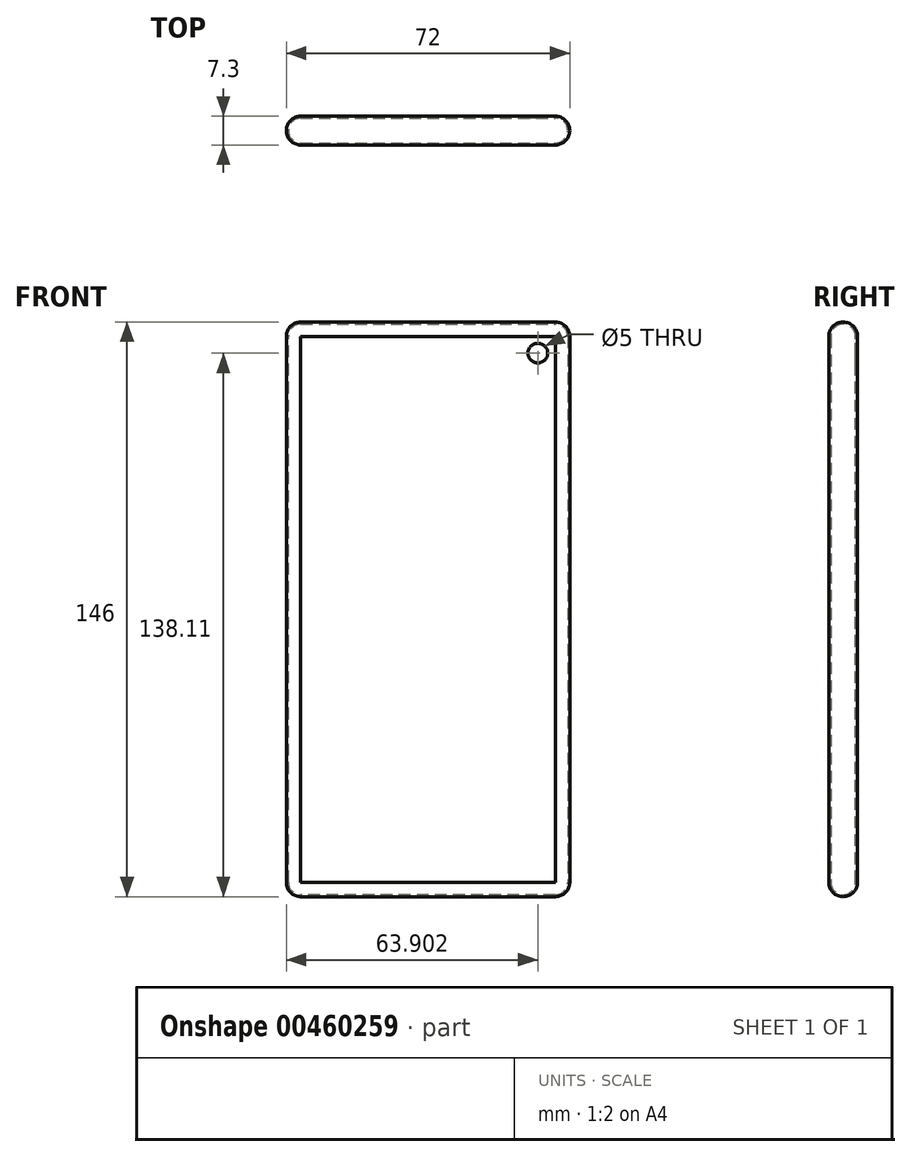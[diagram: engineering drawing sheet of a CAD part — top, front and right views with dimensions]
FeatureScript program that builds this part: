
annotation { "Feature Type Name" : "Feature", "Feature Type Description" : "" }
export const myFeature = defineFeature(function(context is Context, id is Id, definition is map)
    precondition{}
    {
        {
            var Q0;
            Q0=qCreatedBy(makeId("Front.planeOp"),FACE);
            var sketch = newSketch(context, id + "F0", { "sketchPlane" : qUnion([Q0])});
            skLineSegment(sketch, "E0.bottom", {"start": v(36, -73) * mm, "end": v(-36, -73) * mm});
            skLineSegment(sketch, "E0.top", {"start": v(36, 73) * mm, "end": v(-36, 73) * mm});
            skLineSegment(sketch, "E0.left", {"start": v(36, -73) * mm, "end": v(36, 73) * mm});
            skLineSegment(sketch, "E0.right", {"start": v(-36, -73) * mm, "end": v(-36, 73) * mm});
            skPoint(sketch, "E0.middle", {"position": v(0, 0) * mm});
            skSolve(sketch);
        }
        {
            var Q0;
            Q0 = qSketchRegion(id + "F0", true);
            extrude(context, id + "F1", {"entities" : qUnion([Q0]), "depth" : 7.3 * mm, "symmetric" : true});
        }
        {
            var Q0;
            Q0=makeQuery(id+"F1.opExtrude","CAP_EDGE",EDGE,{"disambiguationData":[OSD([sQuery(id+"F0.wireOp",EDGE,"E0.top")])],"isStart":false});
            var Q1;
            Q1=makeQuery(id+"F1.opExtrude","CAP_EDGE",EDGE,{"disambiguationData":[OSD([sQuery(id+"F0.wireOp",EDGE,"E0.top")])],"isStart":true});
            var Q2;
            Q2=makeQuery(id+"F1.opExtrude","CAP_EDGE",EDGE,{"disambiguationData":[OSD([sQuery(id+"F0.wireOp",EDGE,"E0.bottom")])],"isStart":false});
            var Q3;
            Q3=makeQuery(id+"F1.opExtrude","CAP_EDGE",EDGE,{"disambiguationData":[OSD([sQuery(id+"F0.wireOp",EDGE,"E0.bottom")])],"isStart":true});
            var Q4;
            Q4=makeQuery(id+"F1.opExtrude","CAP_EDGE",EDGE,{"disambiguationData":[OSD([sQuery(id+"F0.wireOp",EDGE,"E0.left")])],"isStart":true});
            var Q5;
            Q5=makeQuery(id+"F1.opExtrude","CAP_EDGE",EDGE,{"disambiguationData":[OSD([sQuery(id+"F0.wireOp",EDGE,"E0.left")])],"isStart":false});
            var Q6;
            Q6=makeQuery(id+"F1.opExtrude","SWEPT_FACE",FACE,{"disambiguationData":[OSD([sQuery(id+"F0.wireOp",EDGE,"E0.right")])]});
            var Q7;
            Q7=makeQuery(id+"F1.opExtrude","CAP_EDGE",EDGE,{"disambiguationData":[OSD([sQuery(id+"F0.wireOp",EDGE,"E0.right")])],"isStart":true});
            var Q8;
            Q8=makeQuery(id+"F1.opExtrude","CAP_EDGE",EDGE,{"disambiguationData":[OSD([sQuery(id+"F0.wireOp",EDGE,"E0.right")])],"isStart":false});
            var Q9;
            Q9=makeQuery(id+"F1.opExtrude","SWEPT_EDGE",EDGE,{"disambiguationData":[OSD([sQuery(id+"F0.wireOp",EDGE,"E0.top"),sQuery(id+"F0.wireOp",EDGE,"E0.left")])]});
            var Q10;
            Q10=makeQuery(id+"F1.opExtrude","SWEPT_EDGE",EDGE,{"disambiguationData":[OSD([sQuery(id+"F0.wireOp",EDGE,"E0.bottom"),sQuery(id+"F0.wireOp",EDGE,"E0.left")])]});
            fillet(context, id + "F2", {"entities" : qUnion([Q0, Q1, Q2, Q3, Q4, Q5, Q6, Q7, Q8, Q9, Q10]), "radius" : 3.65 * mm, "tangentPropagation" : true, "allowEdgeOverflow" : false});
        }
        {
            var Q0;
            Q0=makeQuery(id+"F1.opExtrude","CAP_FACE",FACE,{"disambiguationData":[OSD([sQuery(id+"F0.wireOp",EDGE,"E0.bottom"),sQuery(id+"F0.wireOp",EDGE,"E0.top"),sQuery(id+"F0.wireOp",EDGE,"E0.left"),sQuery(id+"F0.wireOp",EDGE,"E0.right")])],"isStart":false});
            shell(context, id + "F3", {"entities" : qUnion([Q0]), "thickness" : 0.5 * mm});
        }
        {
            var Q0;
            Q0=makeQuery(id+"F1.opExtrude","CAP_FACE",FACE,{"disambiguationData":[OSD([sQuery(id+"F0.wireOp",EDGE,"E0.bottom"),sQuery(id+"F0.wireOp",EDGE,"E0.top"),sQuery(id+"F0.wireOp",EDGE,"E0.left"),sQuery(id+"F0.wireOp",EDGE,"E0.right")])],"isStart":true});
            var sketch = newSketch(context, id + "F4", { "sketchPlane" : qUnion([Q0])});
            skCircle(sketch, "E1", {"center": v(-27.9, 65.11) * mm, "radius": 3.04 * mm});
            skSolve(sketch);
        }
        {
            var Q0;
            Q0=sQuery(id+"F4.wireOp",VERTEX,"E1.center");
            var Q1;
            Q1=makeQuery(id+"F1.opExtrude","SWEPT_BODY",BODY,{"disambiguationData":[OSD([sQuery(id+"F0.wireOp",EDGE,"E0.bottom"),sQuery(id+"F0.wireOp",EDGE,"E0.top"),sQuery(id+"F0.wireOp",EDGE,"E0.left"),sQuery(id+"F0.wireOp",EDGE,"E0.right")])]});
            hole(context, id + "F5", {"style" : HoleStyle.SIMPLE, "endStyle" : HoleEndStyle.THROUGH, "holeDiameter" : 5 * mm, "majorDiameter" : 5 * mm, "isTappedThrough" : true, "tappedDepth" : 12 * mm, "tapClearance" : 3, "locations" : qUnion([Q0]), "scope" : qUnion([Q1])});
        }
    });
